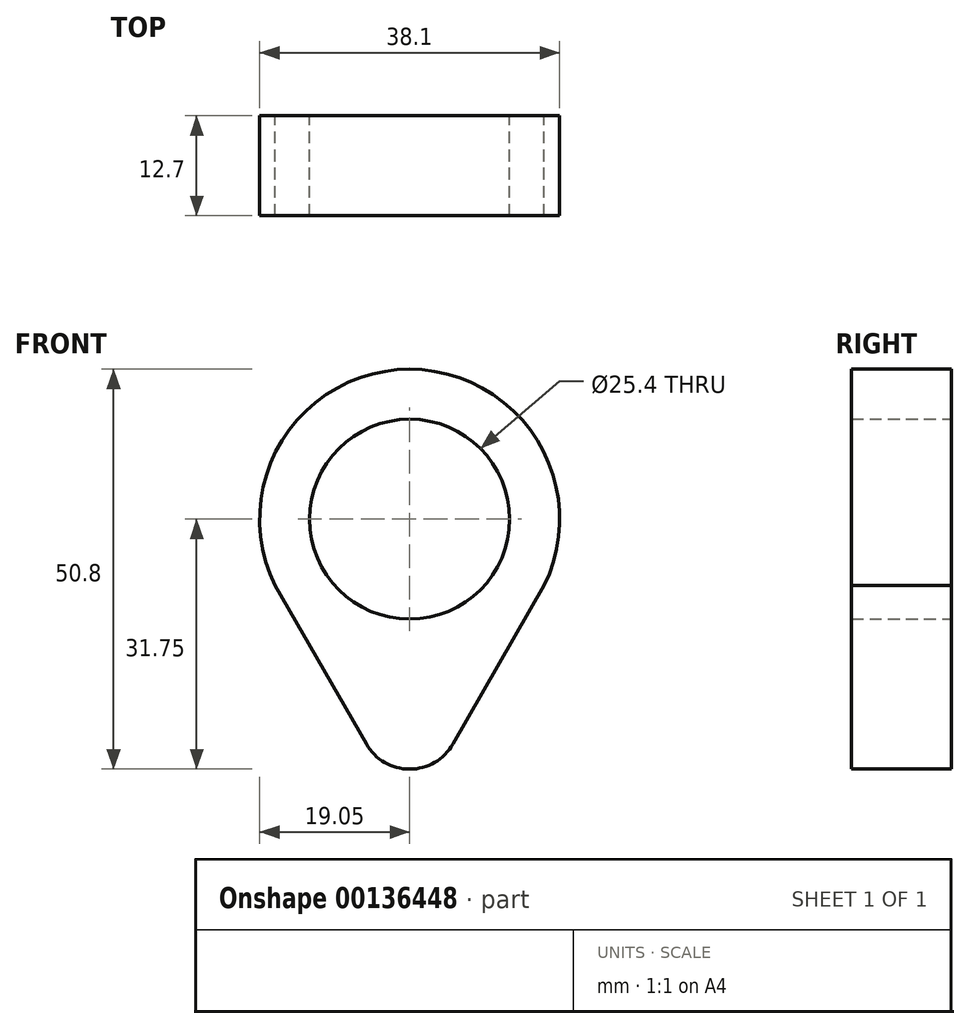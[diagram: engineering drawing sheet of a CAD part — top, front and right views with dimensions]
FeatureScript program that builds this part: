
annotation { "Feature Type Name" : "Feature", "Feature Type Description" : "" }
export const myFeature = defineFeature(function(context is Context, id is Id, definition is map)
    precondition{}
    {
        {
            var Q0;
            Q0=qCreatedBy(makeId("Front.planeOp"),FACE);
            var sketch = newSketch(context, id + "F0", { "sketchPlane" : qUnion([Q0])});
            skCircle(sketch, "E0", {"center": v(0, 0) * mm, "radius": 12.7 * mm});
            skArc(sketch, "E1", {"start": v(-5.5, -28.57) * mm, "mid": v(0, -31.75) * mm, "end": v(5.5, -28.57) * mm});
            skArc(sketch, "E2", {"start": v(17.08, -8.45) * mm, "mid": v(-1.2, 19.01) * mm, "end": v(-15.89, -10.51) * mm});
            skLineSegment(sketch, "E3", {"start": v(-17.08, -8.45) * mm, "end": v(-5.5, -28.57) * mm});
            skLineSegment(sketch, "E4", {"start": v(5.5, -28.57) * mm, "end": v(17.08, -8.45) * mm});
            skSolve(sketch);
        }
        {
            var Q0;
            Q0=makeQuery(id+"F0.imprint","IMPRINT",FACE,{"disambiguationData":[TD([[makeQuery(id+"F0.imprint","IMPRINT",EDGE,{"derivedFrom":sQuery(id+"F0.wireOp",EDGE,"E0")}),-1.0]])]});
            extrude(context, id + "F1", {"entities" : qUnion([Q0]), "depth" : 12.7 * mm});
        }
    });
